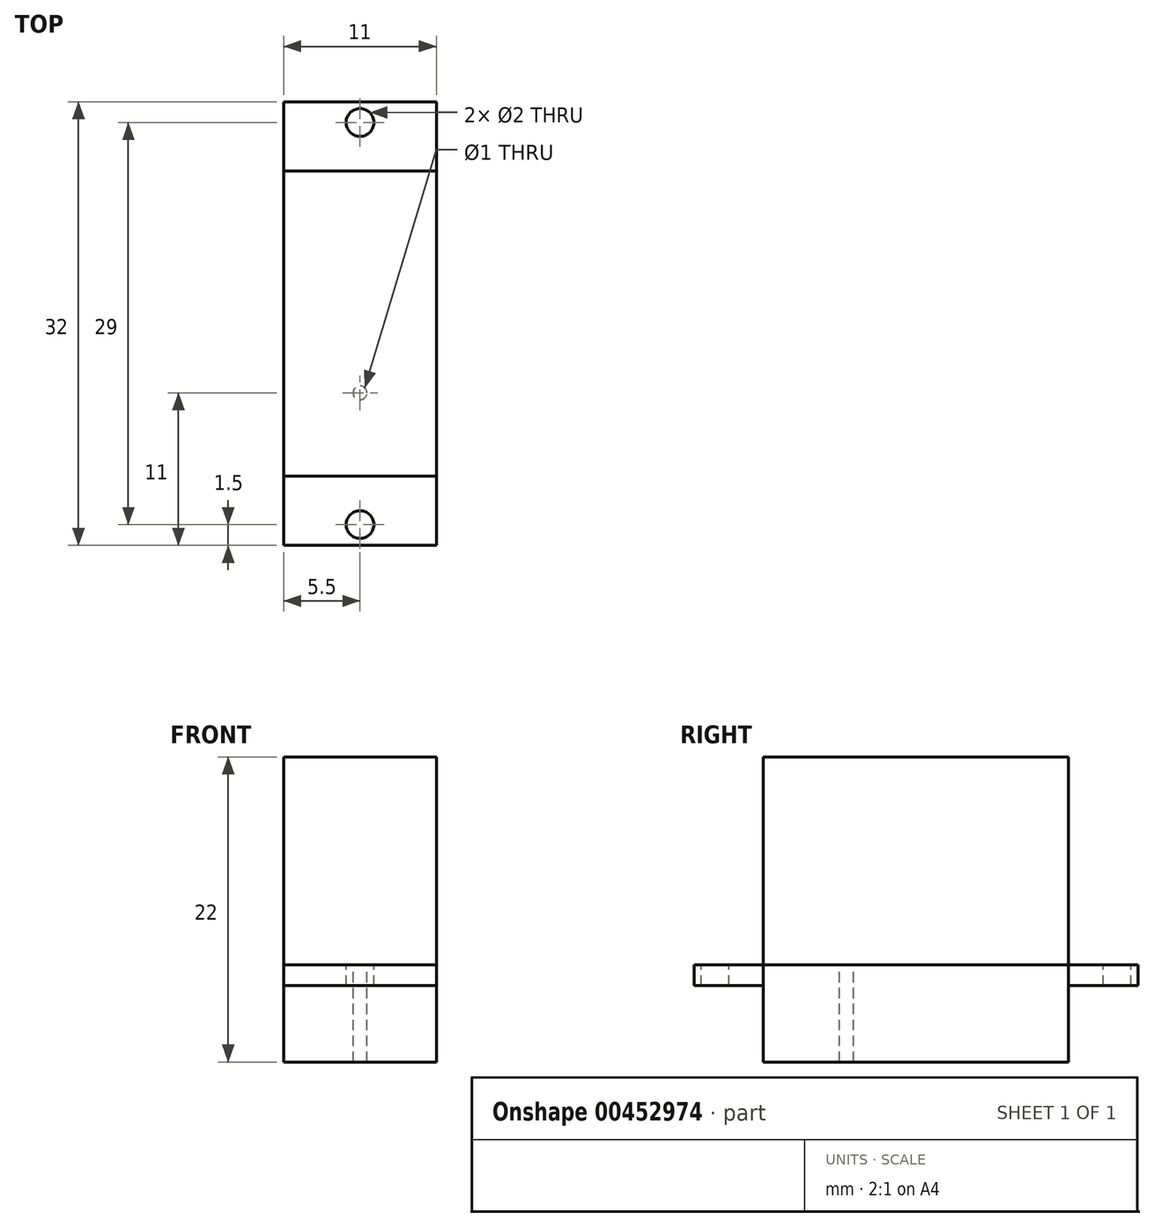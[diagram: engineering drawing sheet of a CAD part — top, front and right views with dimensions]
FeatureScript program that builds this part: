
annotation { "Feature Type Name" : "Feature", "Feature Type Description" : "" }
export const myFeature = defineFeature(function(context is Context, id is Id, definition is map)
    precondition{}
    {
        {
            var Q0;
            Q0=qCreatedBy(makeId("Top.planeOp"),FACE);
            var sketch = newSketch(context, id + "F0", { "sketchPlane" : qUnion([Q0])});
            skLineSegment(sketch, "E0.bottom", {"start": v(-5.5, 11) * mm, "end": v(5.5, 11) * mm});
            skLineSegment(sketch, "E0.top", {"start": v(-5.5, -11) * mm, "end": v(5.5, -11) * mm});
            skLineSegment(sketch, "E0.left", {"start": v(-5.5, 11) * mm, "end": v(-5.5, -11) * mm});
            skLineSegment(sketch, "E0.right", {"start": v(5.5, 11) * mm, "end": v(5.5, -11) * mm});
            skPoint(sketch, "E0.middle", {"position": v(0, 0) * mm});
            skCircle(sketch, "E1", {"center": v(0, 14.5) * mm, "radius": 1 * mm});
            skLineSegment(sketch, "E2.top", {"start": v(-5.5, 16) * mm, "end": v(5.5, 16) * mm});
            skLineSegment(sketch, "E2.left", {"start": v(-5.5, 11) * mm, "end": v(-5.5, 16) * mm});
            skLineSegment(sketch, "E2.right", {"start": v(5.5, 11) * mm, "end": v(5.5, 16) * mm});
            skLineSegment(sketch, "E3.MirrorCS", {"start": v(5.5, -11) * mm, "end": v(5.5, -16) * mm});
            skLineSegment(sketch, "E4.MirrorCS", {"start": v(-5.5, -11) * mm, "end": v(-5.5, -16) * mm});
            skLineSegment(sketch, "E5.MirrorCS", {"start": v(-5.5, -16) * mm, "end": v(5.5, -16) * mm});
            skCircle(sketch, "E6.MirrorC", {"center": v(0, -14.5) * mm, "radius": 1 * mm});
            skCircle(sketch, "E7", {"center": v(0, -5) * mm, "radius": 0.5 * mm});
            skSolve(sketch);
        }
        {
            var Q0;
            Q0=makeQuery(id+"F0.imprint","IMPRINT",FACE,{"disambiguationData":[TD([[makeQuery(id+"F0.imprint","IMPRINT",EDGE,{"derivedFrom":sQuery(id+"F0.wireOp",EDGE,"E0.top")}),1.0]])]});
            var Q1;
            Q1=makeQuery(id+"F0.imprint","IMPRINT",FACE,{"disambiguationData":[TD([[makeQuery(id+"F0.imprint","IMPRINT",EDGE,{"derivedFrom":sQuery(id+"F0.wireOp",EDGE,"E7")}),1.0]])]});
            extrude(context, id + "F1", {"entities" : qUnion([Q0, Q1]), "depth" : 15 * mm});
        }
        {
            var Q0;
            Q0=makeQuery(id+"F0.imprint","IMPRINT",FACE,{"disambiguationData":[TD([[makeQuery(id+"F0.imprint","IMPRINT",EDGE,{"derivedFrom":sQuery(id+"F0.wireOp",EDGE,"E0.top")}),-1.0]])]});
            var Q1;
            Q1=makeQuery(id+"F0.imprint","IMPRINT",FACE,{"disambiguationData":[TD([[makeQuery(id+"F0.imprint","IMPRINT",EDGE,{"derivedFrom":sQuery(id+"F0.wireOp",EDGE,"E1")}),-1.0]])]});
            extrude(context, id + "F2", {"entities" : qUnion([Q0, Q1]), "oppositeDirection" : true, "depth" : 1.5 * mm});
        }
        {
            var Q0;
            Q0=makeQuery(id+"F0.imprint","IMPRINT",FACE,{"disambiguationData":[TD([[makeQuery(id+"F0.imprint","IMPRINT",EDGE,{"derivedFrom":sQuery(id+"F0.wireOp",EDGE,"E0.top")}),1.0]])]});
            extrude(context, id + "F3", {"entities" : qUnion([Q0]), "oppositeDirection" : true, "depth" : 7 * mm});
        }
    });
